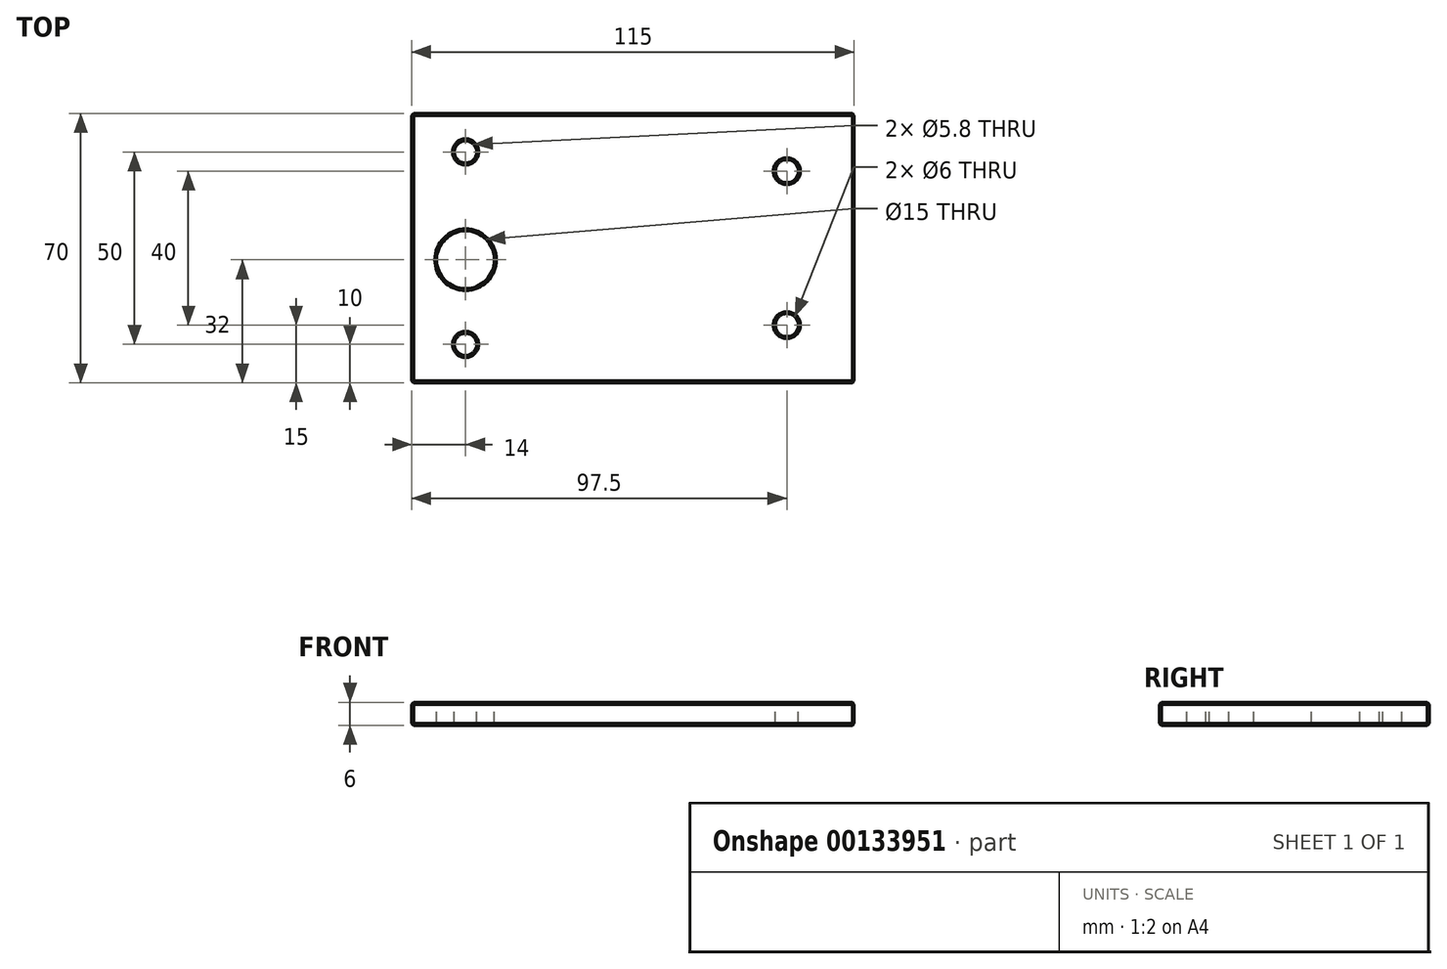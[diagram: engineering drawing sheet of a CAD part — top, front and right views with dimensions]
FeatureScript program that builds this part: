
annotation { "Feature Type Name" : "Feature", "Feature Type Description" : "" }
export const myFeature = defineFeature(function(context is Context, id is Id, definition is map)
    precondition{}
    {
        {
            var Q0;
            Q0=qCreatedBy(makeId("Top.planeOp"),FACE);
            var sketch = newSketch(context, id + "F0", { "sketchPlane" : qUnion([Q0])});
            skLineSegment(sketch, "E0.bottom", {"start": v(57.5, -35) * mm, "end": v(-57.5, -35) * mm});
            skLineSegment(sketch, "E0.top", {"start": v(57.5, 35) * mm, "end": v(-57.5, 35) * mm});
            skLineSegment(sketch, "E0.left", {"start": v(57.5, -35) * mm, "end": v(57.5, 35) * mm});
            skLineSegment(sketch, "E0.right", {"start": v(-57.5, -35) * mm, "end": v(-57.5, 35) * mm});
            skPoint(sketch, "E0.middle", {"position": v(0, 0) * mm});
            skSolve(sketch);
        }
        {
            var Q0;
            Q0=makeQuery(id+"F0.imprint","IMPRINT",FACE,{"disambiguationData":[TD([[makeQuery(id+"F0.imprint","IMPRINT",EDGE,{"derivedFrom":sQuery(id+"F0.wireOp",EDGE,"E0.bottom")}),-1.0]])]});
            extrude(context, id + "F1", {"entities" : qUnion([Q0]), "depth" : 6 * mm, "offsetDistance" : 25 * mm});
        }
        {
            var Q0;
            Q0=makeQuery(id+"F1.opExtrude","CAP_FACE",FACE,{"disambiguationData":[OSD([sQuery(id+"F0.wireOp",EDGE,"E0.bottom"),sQuery(id+"F0.wireOp",EDGE,"E0.top"),sQuery(id+"F0.wireOp",EDGE,"E0.left"),sQuery(id+"F0.wireOp",EDGE,"E0.right")])],"isStart":false});
            var sketch = newSketch(context, id + "F2", { "sketchPlane" : qUnion([Q0])});
            skPoint(sketch, "E1", {"position": v(-43.5, 25) * mm});
            skPoint(sketch, "E2", {"position": v(-43.5, -25) * mm});
            skPoint(sketch, "E3", {"position": v(40, 20) * mm});
            skPoint(sketch, "E4", {"position": v(40, -20) * mm});
            skPoint(sketch, "E5", {"position": v(-43.5, -3) * mm});
            skSolve(sketch);
        }
        {
            var Q0;
            Q0=sQuery(id+"F2.wireOp",VERTEX,"E5");
            var Q1;
            Q1=makeQuery(id+"F1.opExtrude","SWEPT_BODY",BODY,{"disambiguationData":[OSD([sQuery(id+"F0.wireOp",EDGE,"E0.bottom"),sQuery(id+"F0.wireOp",EDGE,"E0.top"),sQuery(id+"F0.wireOp",EDGE,"E0.left"),sQuery(id+"F0.wireOp",EDGE,"E0.right")])]});
            hole(context, id + "F3", {"style" : HoleStyle.SIMPLE, "endStyle" : HoleEndStyle.BLIND, "holeDiameter" : 15 * mm, "majorDiameter" : 5 * mm, "holeDepth" : 20 * mm, "tappedDepth" : 12 * mm, "tapClearance" : 3, "startFromSketch" : true, "locations" : qUnion([Q0]), "scope" : qUnion([Q1])});
        }
        {
            var Q0;
            Q0=sQuery(id+"F2.wireOp",VERTEX,"E1");
            var Q1;
            Q1=sQuery(id+"F2.wireOp",VERTEX,"E2");
            var Q2;
            Q2=makeQuery(id+"F1.opExtrude","SWEPT_BODY",BODY,{"disambiguationData":[OSD([sQuery(id+"F0.wireOp",EDGE,"E0.bottom"),sQuery(id+"F0.wireOp",EDGE,"E0.top"),sQuery(id+"F0.wireOp",EDGE,"E0.left"),sQuery(id+"F0.wireOp",EDGE,"E0.right")])]});
            hole(context, id + "F4", {"style" : HoleStyle.SIMPLE, "endStyle" : HoleEndStyle.BLIND, "holeDiameter" : 5.8 * mm, "majorDiameter" : 5 * mm, "holeDepth" : 20 * mm, "tappedDepth" : 12 * mm, "tapClearance" : 3, "startFromSketch" : true, "locations" : qUnion([Q0, Q1]), "scope" : qUnion([Q2])});
        }
        {
            var Q0;
            Q0=sQuery(id+"F2.wireOp",VERTEX,"E3");
            var Q1;
            Q1=sQuery(id+"F2.wireOp",VERTEX,"E4");
            var Q2;
            Q2=makeQuery(id+"F1.opExtrude","SWEPT_BODY",BODY,{"disambiguationData":[OSD([sQuery(id+"F0.wireOp",EDGE,"E0.bottom"),sQuery(id+"F0.wireOp",EDGE,"E0.top"),sQuery(id+"F0.wireOp",EDGE,"E0.left"),sQuery(id+"F0.wireOp",EDGE,"E0.right")])]});
            hole(context, id + "F5", {"style" : HoleStyle.SIMPLE, "endStyle" : HoleEndStyle.BLIND, "holeDiameter" : 6 * mm, "majorDiameter" : 5 * mm, "holeDepth" : 20 * mm, "tappedDepth" : 12 * mm, "tapClearance" : 3, "startFromSketch" : true, "locations" : qUnion([Q0, Q1]), "scope" : qUnion([Q2])});
        }
        {
            var Q0;
            Q0=makeQuery(id+"F1.opExtrude","CAP_FACE",FACE,{"disambiguationData":[OSD([sQuery(id+"F0.wireOp",EDGE,"E0.bottom"),sQuery(id+"F0.wireOp",EDGE,"E0.top"),sQuery(id+"F0.wireOp",EDGE,"E0.left"),sQuery(id+"F0.wireOp",EDGE,"E0.right")])],"isStart":true});
            var Q1;
            Q1=makeQuery(id+"F1.opExtrude","CAP_FACE",FACE,{"disambiguationData":[OSD([sQuery(id+"F0.wireOp",EDGE,"E0.bottom"),sQuery(id+"F0.wireOp",EDGE,"E0.top"),sQuery(id+"F0.wireOp",EDGE,"E0.left"),sQuery(id+"F0.wireOp",EDGE,"E0.right")])],"isStart":false});
            var Q2;
            Q2=makeQuery(id+"F1.opExtrude","SWEPT_EDGE",EDGE,{"disambiguationData":[OSD([sQuery(id+"F0.wireOp",EDGE,"E0.top"),sQuery(id+"F0.wireOp",EDGE,"E0.left")])]});
            var Q3;
            Q3=makeQuery(id+"F1.opExtrude","SWEPT_EDGE",EDGE,{"disambiguationData":[OSD([sQuery(id+"F0.wireOp",EDGE,"E0.bottom"),sQuery(id+"F0.wireOp",EDGE,"E0.left")])]});
            var Q4;
            Q4=makeQuery(id+"F1.opExtrude","SWEPT_EDGE",EDGE,{"disambiguationData":[OSD([sQuery(id+"F0.wireOp",EDGE,"E0.bottom"),sQuery(id+"F0.wireOp",EDGE,"E0.right")])]});
            var Q5;
            Q5=makeQuery(id+"F1.opExtrude","SWEPT_EDGE",EDGE,{"disambiguationData":[OSD([sQuery(id+"F0.wireOp",EDGE,"E0.top"),sQuery(id+"F0.wireOp",EDGE,"E0.right")])]});
            chamfer(context, id + "F6", {"entities" : qUnion([Q0, Q1, Q2, Q3, Q4, Q5]), "width" : 0.5 * mm, "tangentPropagation" : true});
        }
    });
